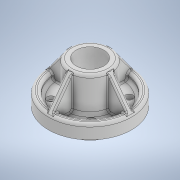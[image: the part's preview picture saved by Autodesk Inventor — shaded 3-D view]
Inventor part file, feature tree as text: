
AUTODESK INVENTOR PART (.ipt)
format: ipt  version: 2022 (Build 260153000, 153)  size: 967,680 bytes
history: native  units: mm
features: sketch x3, other x2, pattern_circular x2, extrude x1, fillet x1, hole x1
ambient origin geometry x8: Origin, YZ Plane, XZ Plane, XY Plane, X Axis, Y Axis, Z Axis, Center Point
bodies: Body1 (feature_tree)
feature tree (10):
  other  "Těleso1"
  other  "Rotace1"
  extrude  "Vysunutí1"  Depth=20.0mm
  fillet  "Zaoblení1"  Radius=20.0mm
  pattern_circular  "Kruhové pole1"  Count=5  [1 undecoded]
  hole  "Díra1"  [1 undecoded]
  pattern_circular  "Kruhové pole2"  Count=4  [1 undecoded]
  sketch  "Náčrt1"
  sketch  "Náčrt2"
  sketch  "Náčrt3"
note: 3 required parameter values undecoded (feature->parameter linkage not recoverable at this tier; creation-order binding heuristic only, values carry confidence <= 0.55)
